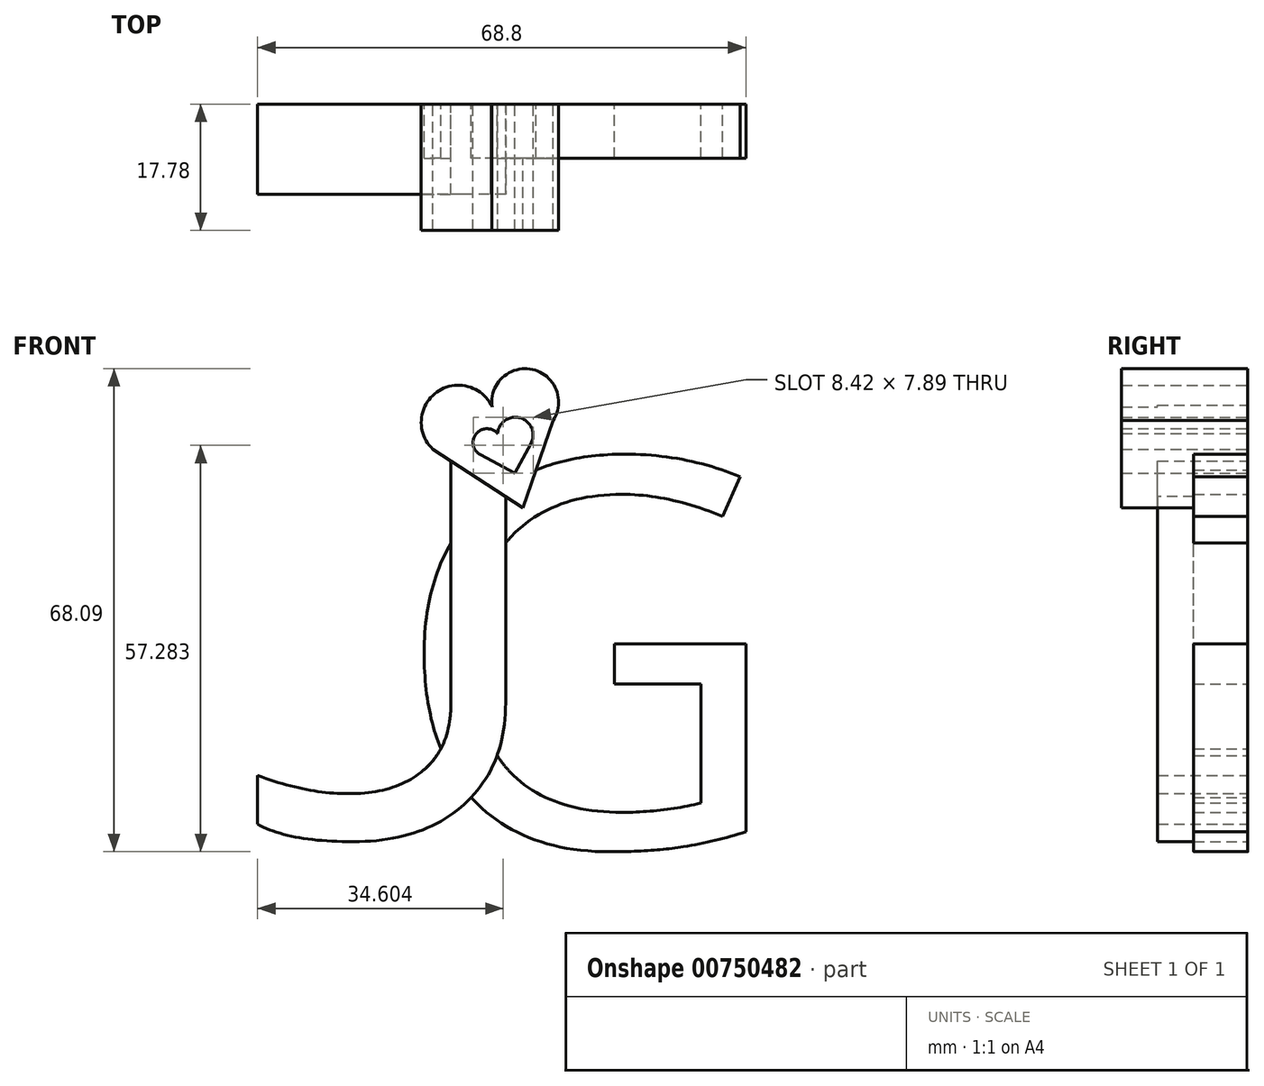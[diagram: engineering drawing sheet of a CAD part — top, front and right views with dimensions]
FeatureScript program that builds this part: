
annotation { "Feature Type Name" : "Feature", "Feature Type Description" : "" }
export const myFeature = defineFeature(function(context is Context, id is Id, definition is map)
    precondition{}
    {
        {
            var Q0;
            Q0=qCreatedBy(makeId("Front.planeOp"),FACE);
            var sketch = newSketch(context, id + "F0", { "sketchPlane" : qUnion([Q0])});
            skText(sketch, "E0", { "text": "J\n", "fontName": "DroidSansMono.ttf"});
            const initialGuessF0  = {"E0": [-0.05824, -0.02258, 1, 0, 0.0612]};
            skSetInitialGuess(sketch, initialGuessF0);
            skSolve(sketch);
        }
        {
            var Q0;
            Q0 = qSketchRegion(id + "F0", true);
            extrude(context, id + "F1", {"entities" : qUnion([Q0]), "depth" : 12.7 * mm, "offsetDistance" : 25.4 * mm});
        }
        {
            var Q0;
            Q0=qCreatedBy(makeId("Front.planeOp"),FACE);
            var sketch = newSketch(context, id + "F2", { "sketchPlane" : qUnion([Q0])});
            skText(sketch, "E1", { "text": "G", "fontName": "OpenSans-Regular.ttf"});
            const initialGuessF2  = {"E1": [-0.03376, -0.02408, 1, 0, 0.05498]};
            skSetInitialGuess(sketch, initialGuessF2);
            skSolve(sketch);
        }
        {
            var Q0;
            Q0 = qSketchRegion(id + "F2", true);
            extrude(context, id + "F3", {"entities" : qUnion([Q0]), "operationType" : NewBodyOperationType.ADD, "depth" : 7.62 * mm, "offsetDistance" : 25.4 * mm});
        }
        {
            var Q0;
            Q0=qCreatedBy(makeId("Front.planeOp"),FACE);
            var sketch = newSketch(context, id + "F4", { "sketchPlane" : qUnion([Q0])});
            skLineSegment(sketch, "E2", {"start": v(-27.87, 31.91) * mm, "end": v(-15.16, 23.64) * mm});
            skLineSegment(sketch, "E3", {"start": v(-15.16, 23.64) * mm, "end": v(-10.93, 35.96) * mm});
            skArc(sketch, "E4", {"start": v(-19.12, 36.53) * mm, "mid": v(-26.72, 40.33) * mm, "end": v(-27.87, 31.91) * mm});
            skArc(sketch, "E5", {"start": v(-10.93, 35.96) * mm, "mid": v(-14.53, 43.25) * mm, "end": v(-19.12, 36.53) * mm});
            skSolve(sketch);
        }
        {
            var Q0;
            Q0 = qSketchRegion(id + "F4", true);
            extrude(context, id + "F5", {"entities" : qUnion([Q0]), "operationType" : NewBodyOperationType.ADD, "depth" : 17.78 * mm, "offsetDistance" : 25.4 * mm});
        }
        {
            var Q0;
            Q0=qCreatedBy(makeId("Front.planeOp"),FACE);
            var sketch = newSketch(context, id + "F6", { "sketchPlane" : qUnion([Q0])});
            skLineSegment(sketch, "E6", {"start": v(-16.32, 28.5) * mm, "end": v(-21.17, 31.12) * mm});
            skLineSegment(sketch, "E7", {"start": v(-16.32, 28.5) * mm, "end": v(-14.04, 32.74) * mm});
            skArc(sketch, "E8", {"start": v(-18.75, 34.1) * mm, "mid": v(-21.76, 34.08) * mm, "end": v(-21.17, 31.12) * mm});
            skPoint(sketch, "E8.startSnap0", {"position": v(-18.75, 29.82) * mm});
            skArc(sketch, "E9", {"start": v(-14.04, 32.74) * mm, "mid": v(-15.55, 36.33) * mm, "end": v(-18.75, 34.1) * mm});
            skSolve(sketch);
        }
        {
            var Q0;
            Q0 = qSketchRegion(id + "F6", true);
            extrude(context, id + "F7", {"entities" : qUnion([Q0]), "operationType" : NewBodyOperationType.REMOVE, "depth" : 76.2 * mm, "offsetDistance" : 25.4 * mm});
        }
    });
